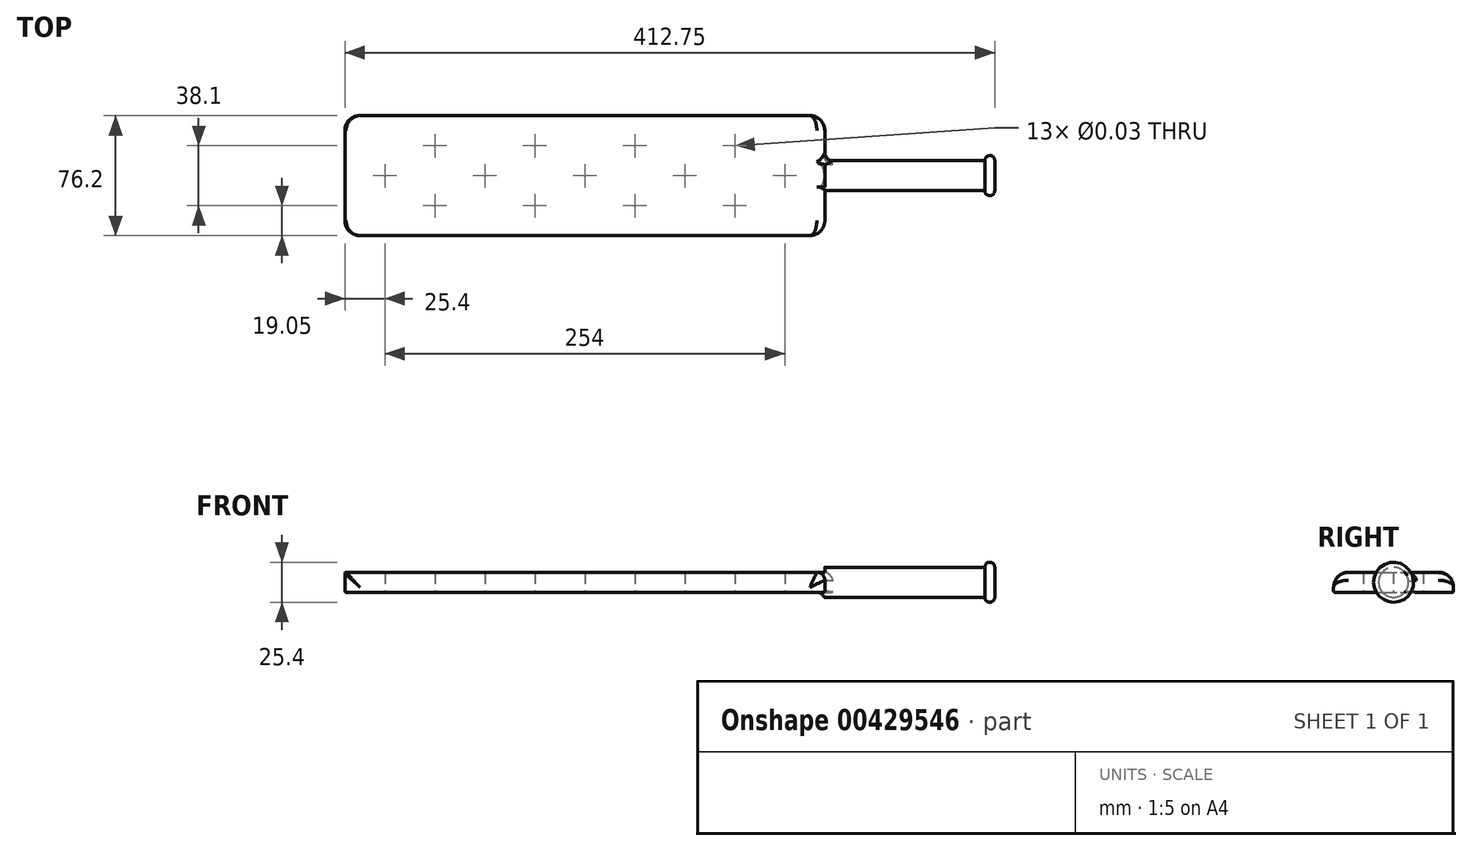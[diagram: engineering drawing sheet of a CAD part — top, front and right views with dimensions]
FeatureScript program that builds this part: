
annotation { "Feature Type Name" : "Feature", "Feature Type Description" : "" }
export const myFeature = defineFeature(function(context is Context, id is Id, definition is map)
    precondition{}
    {
        {
            var Q0;
            Q0=qCreatedBy(makeId("Top.planeOp"),FACE);
            var sketch = newSketch(context, id + "F0", { "sketchPlane" : qUnion([Q0])});
            skLineSegment(sketch, "E0.bottom", {"start": v(152.4, -38.1) * mm, "end": v(-152.4, -38.1) * mm});
            skLineSegment(sketch, "E0.top", {"start": v(152.4, 38.1) * mm, "end": v(-152.4, 38.1) * mm});
            skLineSegment(sketch, "E0.left", {"start": v(152.4, -38.1) * mm, "end": v(152.4, 38.1) * mm});
            skLineSegment(sketch, "E0.right", {"start": v(-152.4, -38.1) * mm, "end": v(-152.4, 38.1) * mm});
            skPoint(sketch, "E0.middle", {"position": v(0, 0) * mm});
            skSolve(sketch);
        }
        {
            var Q0;
            Q0=makeQuery(id+"F0.imprint","IMPRINT",FACE,{"disambiguationData":[TD([[makeQuery(id+"F0.imprint","IMPRINT",EDGE,{"derivedFrom":sQuery(id+"F0.wireOp",EDGE,"E0.bottom")}),-1.0]])]});
            extrude(context, id + "F1", {"entities" : qUnion([Q0]), "endBound" : BoundingType.SYMMETRIC, "depth" : 12.7 * mm});
        }
        {
            var Q0;
            Q0=makeQuery(id+"F1.opExtrude","SWEPT_FACE",FACE,{"disambiguationData":[OSD([sQuery(id+"F0.wireOp",EDGE,"E0.left")])]});
            var sketch = newSketch(context, id + "F2", { "sketchPlane" : qUnion([Q0])});
            skCircle(sketch, "E1", {"center": v(0, 0) * mm, "radius": 9.53 * mm});
            skSolve(sketch);
        }
        {
            var Q0;
            Q0 = qSketchRegion(id + "F2", true);
            extrude(context, id + "F3", {"entities" : qUnion([Q0]), "operationType" : NewBodyOperationType.ADD, "depth" : 101.6 * mm});
        }
        {
            var Q0;
            Q0=qCreatedBy(makeId("Front.planeOp"),FACE);
            var sketch = newSketch(context, id + "F4", { "sketchPlane" : qUnion([Q0])});
            skLineSegment(sketch, "E2.0", {"start": v(254, 9.53) * mm, "end": v(254, -9.53) * mm, "construction": true});
            skArc(sketch, "E3", {"start": v(254, 9.53) * mm, "mid": v(257.18, 12.7) * mm, "end": v(260.35, 9.53) * mm});
            skLineSegment(sketch, "E4", {"start": v(260.35, 9.53) * mm, "end": v(260.35, 0) * mm});
            skLineSegment(sketch, "E5", {"start": v(260.35, 0) * mm, "end": v(254, 0) * mm});
            skLineSegment(sketch, "E6", {"start": v(254, 0) * mm, "end": v(254, 9.53) * mm});
            skSolve(sketch);
        }
        {
            var Q0;
            Q0 = qSketchRegion(id + "F4", true);
            var Q1;
            Q1=makeQuery(id+"F3.opExtrude","SWEPT_FACE",FACE,{"disambiguationData":[OSD([sQuery(id+"F2.wireOp",EDGE,"E1")])]});
            revolve(context, id + "F5", {"operationType" : NewBodyOperationType.ADD, "entities" : qUnion([Q0]), "axis" : qUnion([Q1]), "revolveType" : RevolveType.FULL});
        }
        {
            var Q0;
            {var subQ0=sQuery(id+"F0.wireOp",EDGE,"E0.left");Q0=makeQuery(id+"F3.boolean.opBoolean","SPLIT",EDGE,{"disambiguationData":[topologyDisambiguationEdgeConnected([makeQuery(id+"F1.opExtrude","CAP_FACE",FACE,{"disambiguationData":[OSD([sQuery(id+"F0.wireOp",EDGE,"E0.bottom"),sQuery(id+"F0.wireOp",EDGE,"E0.top"),subQ0,sQuery(id+"F0.wireOp",EDGE,"E0.right")])],"isStart":false}),makeQuery(id+"F3.opExtrude","CAP_FACE",FACE,{"disambiguationData":[OSD([sQuery(id+"F2.wireOp",EDGE,"E1")])],"isStart":true})])],"derivedFrom":makeQuery(id+"F1.opExtrude","CAP_EDGE",EDGE,{"disambiguationData":[OSD([subQ0])],"isStart":false})});}
            var Q1;
            {var subQ0=sQuery(id+"F0.wireOp",EDGE,"E0.left");Q1=makeQuery(id+"F3.boolean.opBoolean","SPLIT",EDGE,{"disambiguationData":[topologyDisambiguationEdgeConnected([makeQuery(id+"F1.opExtrude","CAP_FACE",FACE,{"disambiguationData":[OSD([sQuery(id+"F0.wireOp",EDGE,"E0.bottom"),sQuery(id+"F0.wireOp",EDGE,"E0.top"),subQ0,sQuery(id+"F0.wireOp",EDGE,"E0.right")])],"isStart":true}),makeQuery(id+"F3.opExtrude","CAP_FACE",FACE,{"disambiguationData":[OSD([sQuery(id+"F2.wireOp",EDGE,"E1")])],"isStart":true})])],"derivedFrom":makeQuery(id+"F1.opExtrude","CAP_EDGE",EDGE,{"disambiguationData":[OSD([subQ0])],"isStart":true})});}
            fillet(context, id + "F6", {"entities" : qUnion([Q0, Q1]), "radius" : 5.08 * mm, "tangentPropagation" : true, "allowEdgeOverflow" : false});
        }
        {
            var Q0;
            {var subQ0=sQuery(id+"F2.wireOp",EDGE,"E1");Q0=makeQuery(id+"F3.boolean.opBoolean","SPLIT",EDGE,{"disambiguationData":[topologyDisambiguationEdgeConnected([makeQuery(id+"F1.opExtrude","SWEPT_FACE",FACE,{"disambiguationData":[OSD([sQuery(id+"F0.wireOp",EDGE,"E0.left")])]}),makeQuery(id+"F3.opExtrude","SWEPT_FACE",FACE,{"disambiguationData":[OSD([subQ0])]})]),OD(0.0)],"derivedFrom":makeQuery(id+"F3.opExtrude","CAP_EDGE",EDGE,{"disambiguationData":[OSD([subQ0])],"isStart":true})});}
            var Q1;
            {var subQ0=sQuery(id+"F2.wireOp",EDGE,"E1");Q1=makeQuery(id+"F3.boolean.opBoolean","SPLIT",EDGE,{"disambiguationData":[topologyDisambiguationEdgeConnected([makeQuery(id+"F1.opExtrude","SWEPT_FACE",FACE,{"disambiguationData":[OSD([sQuery(id+"F0.wireOp",EDGE,"E0.left")])]}),makeQuery(id+"F3.opExtrude","SWEPT_FACE",FACE,{"disambiguationData":[OSD([subQ0])]})]),OD(1.0)],"derivedFrom":makeQuery(id+"F3.opExtrude","CAP_EDGE",EDGE,{"disambiguationData":[OSD([subQ0])],"isStart":true})});}
            fillet(context, id + "F7", {"entities" : qUnion([Q0, Q1]), "radius" : 5.08 * mm, "tangentPropagation" : true, "allowEdgeOverflow" : false});
        }
        {
            var Q0;
            Q0=makeQuery(id+"F1.opExtrude","SWEPT_EDGE",EDGE,{"disambiguationData":[OSD([sQuery(id+"F0.wireOp",EDGE,"E0.bottom"),sQuery(id+"F0.wireOp",EDGE,"E0.left")])]});
            var Q1;
            Q1=makeQuery(id+"F1.opExtrude","SWEPT_EDGE",EDGE,{"disambiguationData":[OSD([sQuery(id+"F0.wireOp",EDGE,"E0.top"),sQuery(id+"F0.wireOp",EDGE,"E0.left")])]});
            var Q2;
            Q2=makeQuery(id+"F1.opExtrude","SWEPT_EDGE",EDGE,{"disambiguationData":[OSD([sQuery(id+"F0.wireOp",EDGE,"E0.bottom"),sQuery(id+"F0.wireOp",EDGE,"E0.right")])]});
            var Q3;
            Q3=makeQuery(id+"F1.opExtrude","SWEPT_EDGE",EDGE,{"disambiguationData":[OSD([sQuery(id+"F0.wireOp",EDGE,"E0.top"),sQuery(id+"F0.wireOp",EDGE,"E0.right")])]});
            fillet(context, id + "F8", {"entities" : qUnion([Q0, Q1, Q2, Q3]), "radius" : 9.52 * mm, "tangentPropagation" : true, "allowEdgeOverflow" : false});
        }
        {
            var Q0;
            Q0=makeQuery(id+"F1.opExtrude","CAP_EDGE",EDGE,{"disambiguationData":[OSD([sQuery(id+"F0.wireOp",EDGE,"E0.right")])],"isStart":false});
            var Q1;
            Q1=makeQuery(id+"F1.opExtrude","CAP_EDGE",EDGE,{"disambiguationData":[OSD([sQuery(id+"F0.wireOp",EDGE,"E0.right")])],"isStart":true});
            fillet(context, id + "F9", {"entities" : qUnion([Q0, Q1]), "radius" : 0.79 * mm, "tangentPropagation" : true, "allowEdgeOverflow" : false});
        }
        {
            var Q0;
            Q0=makeQuery(id+"F1.opExtrude","CAP_FACE",FACE,{"disambiguationData":[OSD([sQuery(id+"F0.wireOp",EDGE,"E0.bottom"),sQuery(id+"F0.wireOp",EDGE,"E0.top"),sQuery(id+"F0.wireOp",EDGE,"E0.left"),sQuery(id+"F0.wireOp",EDGE,"E0.right")])],"isStart":true});
            var sketch = newSketch(context, id + "F10", { "sketchPlane" : qUnion([Q0])});
            skPoint(sketch, "E7", {"position": v(-127, 0) * mm});
            skPoint(sketch, "E8", {"position": v(-63.5, 0) * mm});
            skPoint(sketch, "E9", {"position": v(0, 0) * mm});
            skPoint(sketch, "E10", {"position": v(63.5, 0) * mm});
            skPoint(sketch, "E11", {"position": v(127, 0) * mm});
            skPoint(sketch, "E12", {"position": v(-95.25, 19.05) * mm});
            skPoint(sketch, "E13", {"position": v(-95.25, -19.05) * mm});
            skPoint(sketch, "E14", {"position": v(-31.75, -19.05) * mm});
            skPoint(sketch, "E15", {"position": v(-31.75, 19.05) * mm});
            skPoint(sketch, "E16", {"position": v(31.75, 19.05) * mm});
            skPoint(sketch, "E17", {"position": v(31.75, -19.05) * mm});
            skPoint(sketch, "E18", {"position": v(95.25, -19.05) * mm});
            skPoint(sketch, "E19", {"position": v(95.25, 19.05) * mm});
            skSolve(sketch);
        }
        {
            var Q0;
            Q0=sQuery(id+"F10.wireOp",VERTEX,"E12");
            var Q1;
            Q1=sQuery(id+"F10.wireOp",VERTEX,"E7");
            var Q2;
            Q2=sQuery(id+"F10.wireOp",VERTEX,"E8");
            var Q3;
            Q3=sQuery(id+"F10.wireOp",VERTEX,"E15");
            var Q4;
            Q4=sQuery(id+"F10.wireOp",VERTEX,"E16");
            var Q5;
            Q5=sQuery(id+"F10.wireOp",VERTEX,"E9");
            var Q6;
            Q6=sQuery(id+"F10.wireOp",VERTEX,"E10");
            var Q7;
            Q7=sQuery(id+"F10.wireOp",VERTEX,"E19");
            var Q8;
            Q8=sQuery(id+"F10.wireOp",VERTEX,"E11");
            var Q9;
            Q9=sQuery(id+"F10.wireOp",VERTEX,"E13");
            var Q10;
            Q10=sQuery(id+"F10.wireOp",VERTEX,"E14");
            var Q11;
            Q11=sQuery(id+"F10.wireOp",VERTEX,"E17");
            var Q12;
            Q12=sQuery(id+"F10.wireOp",VERTEX,"E18");
            var Q13;
            Q13=makeQuery(id+"F1.opExtrude","SWEPT_BODY",BODY,{"disambiguationData":[OSD([sQuery(id+"F0.wireOp",EDGE,"E0.bottom"),sQuery(id+"F0.wireOp",EDGE,"E0.top"),sQuery(id+"F0.wireOp",EDGE,"E0.left"),sQuery(id+"F0.wireOp",EDGE,"E0.right")])]});
            hole(context, id + "F11", {"style" : HoleStyle.SIMPLE, "endStyle" : HoleEndStyle.THROUGH, "standardTappedOrClearance" : lookupTablePath({ "standard" : "ANSI", "size" : "3/4 (0.75)", "type" : "Drilled" }), "standardBlindInLast" : lookupTablePath({ "standard" : "ANSI", "size" : "3/4", "type" : "Drilled" }), "holeDiameter" : 3 / 101.6 * mm, "isTappedThrough" : true, "tappedDepth" : 12.7 * mm, "tapClearance" : 3, "locations" : qUnion([Q0, Q1, Q2, Q3, Q4, Q5, Q6, Q7, Q8, Q9, Q10, Q11, Q12]), "scope" : qUnion([Q13])});
        }
    });
